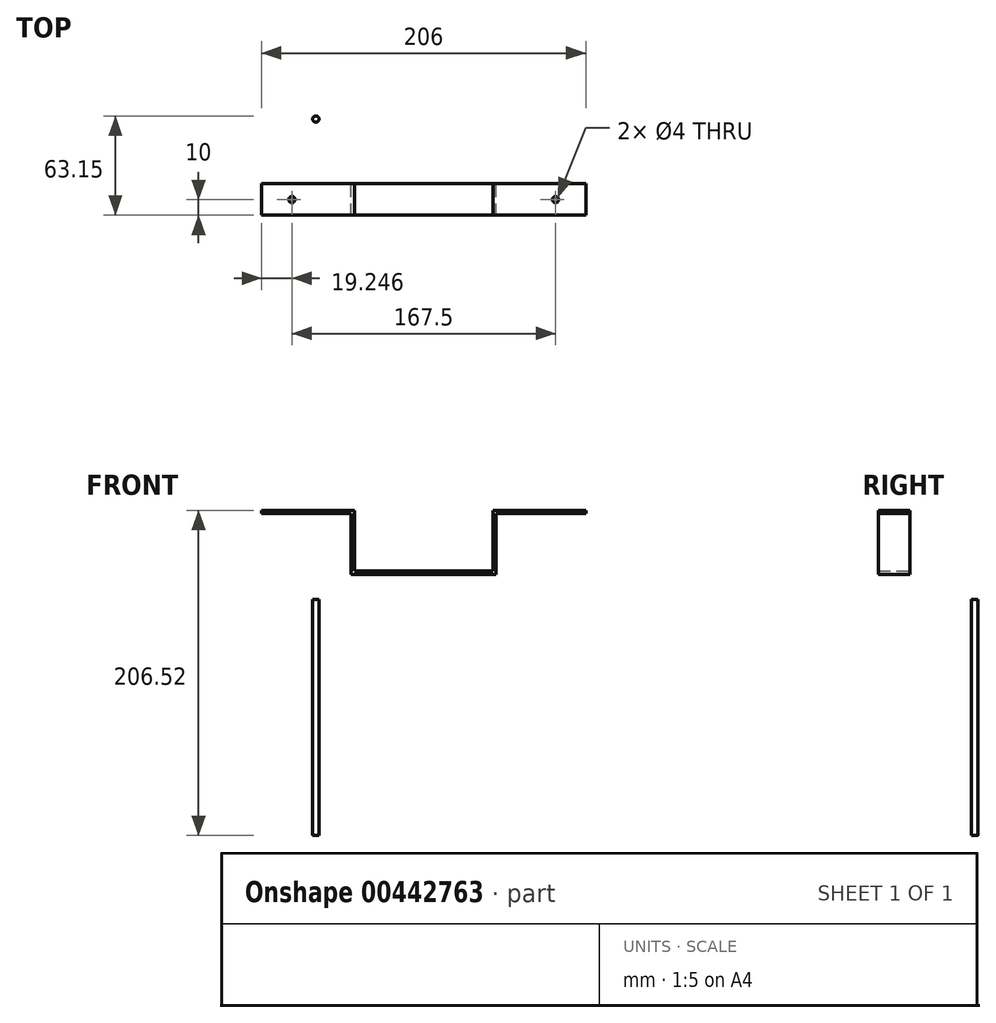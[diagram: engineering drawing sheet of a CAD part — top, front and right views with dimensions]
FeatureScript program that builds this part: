
annotation { "Feature Type Name" : "Feature", "Feature Type Description" : "" }
export const myFeature = defineFeature(function(context is Context, id is Id, definition is map)
    precondition{}
    {
        {
            var Q0;
            Q0=qCreatedBy(makeId("Top.planeOp"),FACE);
            var sketch = newSketch(context, id + "F0", { "sketchPlane" : qUnion([Q0])});
            skCircle(sketch, "E0", {"center": v(-83, 41.15) * mm, "radius": 2 * mm});
            skCircle(sketch, "E1.MirrorC", {"center": v(83, 41.15) * mm, "radius": 2 * mm});
            skSolve(sketch);
        }
        {
            var Q0;
            Q0 = qSketchRegion(id + "F0", true);
            var Q1;
            Q1=sQuery(id+"F0.wireOp",EDGE,"E0");
            extrude(context, id + "F1", {"entities" : qUnion([Q0]), "surfaceEntities" : qUnion([Q1]), "oppositeDirection" : true, "depth" : 150 * mm, "offsetDistance" : 25 * mm});
        }
        {
            var Q0;
            Q0=qCreatedBy(makeId("Front.planeOp"),FACE);
            var sketch = newSketch(context, id + "F2", { "sketchPlane" : qUnion([Q0])});
            skLineSegment(sketch, "E2", {"start": v(88.49, 54.52) * mm, "end": v(31.49, 54.52) * mm});
            skLineSegment(sketch, "E3", {"start": v(31.49, 54.52) * mm, "end": v(31.49, 16.02) * mm});
            skLineSegment(sketch, "E4", {"start": v(31.49, 16.02) * mm, "end": v(-60.51, 16.02) * mm});
            skLineSegment(sketch, "E5", {"start": v(-60.51, 16.02) * mm, "end": v(-60.51, 54.52) * mm});
            skLineSegment(sketch, "E6", {"start": v(-60.51, 54.52) * mm, "end": v(-117.51, 54.52) * mm});
            skLineSegment(sketch, "E7", {"start": v(-117.51, 54.52) * mm, "end": v(-117.51, 56.52) * mm});
            skLineSegment(sketch, "E8", {"start": v(-117.51, 56.52) * mm, "end": v(-58.51, 56.52) * mm});
            skLineSegment(sketch, "E9", {"start": v(-58.51, 56.52) * mm, "end": v(-58.51, 18.02) * mm});
            skLineSegment(sketch, "E10", {"start": v(-58.51, 18.02) * mm, "end": v(29.49, 18.02) * mm});
            skLineSegment(sketch, "E11", {"start": v(29.49, 18.02) * mm, "end": v(29.49, 56.52) * mm});
            skLineSegment(sketch, "E12", {"start": v(29.49, 56.52) * mm, "end": v(88.49, 56.52) * mm});
            skLineSegment(sketch, "E13", {"start": v(88.49, 56.52) * mm, "end": v(88.49, 54.52) * mm});
            skSolve(sketch);
        }
        {
            var Q0;
            Q0 = qSketchRegion(id + "F2", true);
            extrude(context, id + "F3", {"entities" : qUnion([Q0]), "depth" : 20 * mm, "offsetDistance" : 25 * mm});
        }
        {
            var Q0;
            Q0=makeQuery(id+"F3.opExtrude","SWEPT_FACE",FACE,{"disambiguationData":[OSD([sQuery(id+"F2.wireOp",EDGE,"E12")])]});
            var sketch = newSketch(context, id + "F4", { "sketchPlane" : qUnion([Q0])});
            skCircle(sketch, "E14", {"center": v(69.24, -10) * mm, "radius": 2 * mm});
            skPoint(sketch, "E14.centerSnap0", {"position": v(88.49, -10) * mm});
            skCircle(sketch, "E15", {"center": v(-98.26, -10) * mm, "radius": 2 * mm});
            skSolve(sketch);
        }
        {
            var Q0;
            Q0 = qSketchRegion(id + "F4", true);
            extrude(context, id + "F5", {"entities" : qUnion([Q0]), "operationType" : NewBodyOperationType.REMOVE, "oppositeDirection" : true, "depth" : 25 * mm, "offsetDistance" : 25 * mm});
        }
        {
            var Q0;
            Q0=makeQuery(id+"F1.opExtrude","SWEPT_BODY",BODY,{"disambiguationData":[OSD([sQuery(id+"F0.wireOp",EDGE,"E1.MirrorC")])]});
            deleteBodies(context, id + "F6", {"entities" : qUnion([Q0])});
        }
        {
            var Q0;
            Q0=makeQuery(id+"F1.opExtrude","SWEPT_BODY",BODY,{"disambiguationData":[OSD([sQuery(id+"F0.wireOp",EDGE,"E0")])]});
            transform(context, id + "F7", {"entities" : qUnion([Q0]), "transformType" : TransformType.TRANSLATION_3D, "dx" : 0 * mm, "dy" : 0 * mm, "dz" : 0 * mm, "makeCopy" : true});
        }
    });
